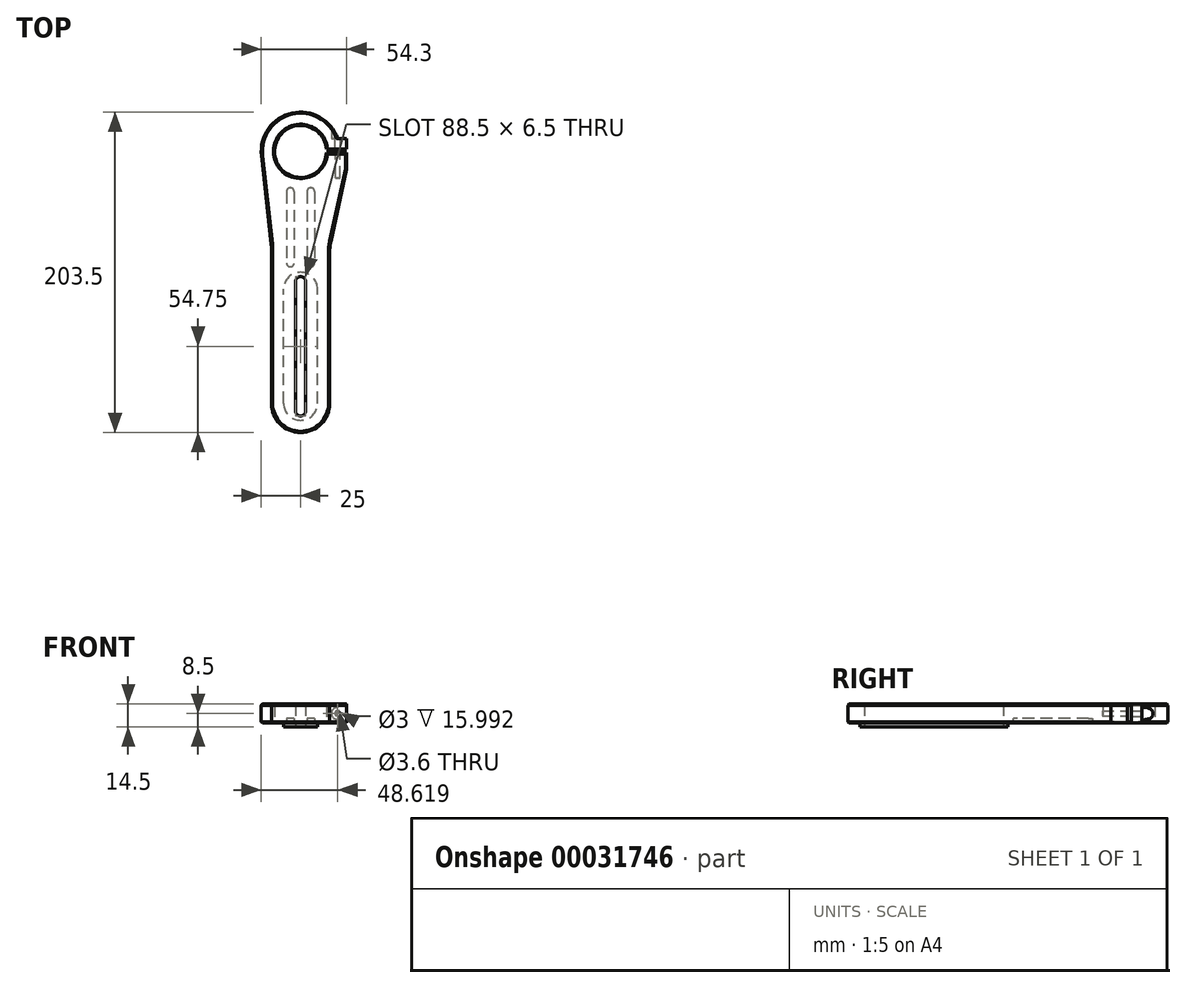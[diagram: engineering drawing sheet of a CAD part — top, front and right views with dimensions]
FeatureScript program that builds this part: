
annotation { "Feature Type Name" : "Feature", "Feature Type Description" : "" }
export const myFeature = defineFeature(function(context is Context, id is Id, definition is map)
    precondition{}
    {
        {
            var Q0;
            Q0=qCreatedBy(makeId("Top.planeOp"),FACE);
            var sketch = newSketch(context, id + "F0", { "sketchPlane" : qUnion([Q0])});
            skLineSegment(sketch, "E0.left", {"start": v(0, 0) * mm, "end": v(0, 99.61) * mm});
            skLineSegment(sketch, "E0.right", {"start": v(37, 0) * mm, "end": v(37, 99.61) * mm});
            skArc(sketch, "E1", {"start": v(0, 0) * mm, "mid": v(18.5, -18.5) * mm, "end": v(37, 0) * mm});
            skLineSegment(sketch, "E2", {"start": v(0, 99.61) * mm, "end": v(-6.35, 157.26) * mm});
            skArc(sketch, "E3", {"start": v(34.92, 161.59) * mm, "mid": v(2, 159.61) * mm, "end": v(34.98, 159.19) * mm});
            skLineSegment(sketch, "E4", {"start": v(34.92, 161.59) * mm, "end": v(47.8, 161.59) * mm});
            skLineSegment(sketch, "E5", {"start": v(34.98, 159.19) * mm, "end": v(47.8, 159.19) * mm});
            skArc(sketch, "E6.trimOffspring", {"start": v(42.12, 168.2) * mm, "mid": v(13, 184.39) * mm, "end": v(-6.35, 157.26) * mm});
            skLineSegment(sketch, "E7.trimOffspring", {"start": v(47.8, 159.19) * mm, "end": v(47.8, 148.78) * mm});
            skLineSegment(sketch, "E8", {"start": v(37, 99.61) * mm, "end": v(47.8, 148.78) * mm});
            skLineSegment(sketch, "E9", {"start": v(47.8, 168.2) * mm, "end": v(42.12, 168.2) * mm});
            skLineSegment(sketch, "E10", {"start": v(47.8, 168.2) * mm, "end": v(47.8, 161.59) * mm});
            skSolve(sketch);
        }
        {
            var Q0;
            Q0=makeQuery(id+"F0.imprint","IMPRINT",FACE,{"disambiguationData":[TD([[makeQuery(id+"F0.imprint","IMPRINT",EDGE,{"derivedFrom":sQuery(id+"F0.wireOp",EDGE,"E0.left")}),-1.0]])]});
            extrude(context, id + "F1", {"entities" : qUnion([Q0]), "depth" : 12 * mm});
        }
        {
            var Q0;
            Q0=makeQuery(id+"F1.opExtrude","CAP_FACE",FACE,{"disambiguationData":[OSD([sQuery(id+"F0.wireOp",EDGE,"E0.left"),sQuery(id+"F0.wireOp",EDGE,"E0.right"),sQuery(id+"F0.wireOp",EDGE,"E1"),sQuery(id+"F0.wireOp",EDGE,"17b39365-8552-41ff-bf17-2f0143301558"),sQuery(id+"F0.wireOp",EDGE,"c914b5d8-53f2-4ac4-93b2-2ecc952be14a")])],"isStart":true});
            var sketch = newSketch(context, id + "F2", { "sketchPlane" : qUnion([Q0])});
            skLineSegment(sketch, "E11.left", {"start": v(7.7, 0) * mm, "end": v(7.7, -72.5) * mm});
            skLineSegment(sketch, "E11.right", {"start": v(29.3, 0) * mm, "end": v(29.3, -72.5) * mm});
            skLineSegment(sketch, "E12", {"start": v(18.5, 153.67) * mm, "end": v(18.5, -165.42) * mm, "construction": true});
            skArc(sketch, "E13", {"start": v(29.3, 0) * mm, "mid": v(18.5, 10.8) * mm, "end": v(7.7, 0) * mm});
            skArc(sketch, "E14", {"start": v(7.7, -72.5) * mm, "mid": v(18.5, -83.3) * mm, "end": v(29.3, -72.5) * mm});
            skSolve(sketch);
        }
        {
            var Q0;
            Q0=qSketchRegion(id+"F2",true);
            extrude(context, id + "F3", {"entities" : qUnion([Q0]), "operationType" : NewBodyOperationType.ADD, "depth" : 2.5 * mm});
        }
        {
            var Q0;
            Q0=makeQuery(id+"F3.opExtrude","CAP_FACE",FACE,{"disambiguationData":[OSD([sQuery(id+"F2.wireOp",EDGE,"E11.left"),sQuery(id+"F2.wireOp",EDGE,"E11.right"),sQuery(id+"F2.wireOp",EDGE,"E13"),sQuery(id+"F2.wireOp",EDGE,"E14")])],"isStart":false});
            var sketch = newSketch(context, id + "F4", { "sketchPlane" : qUnion([Q0])});
            skLineSegment(sketch, "E15.left", {"start": v(15.25, 4.75) * mm, "end": v(15.25, -77.25) * mm});
            skLineSegment(sketch, "E15.right", {"start": v(21.75, 4.75) * mm, "end": v(21.75, -77.25) * mm});
            skArc(sketch, "E16", {"start": v(21.75, 4.75) * mm, "mid": v(18.5, 8) * mm, "end": v(15.25, 4.75) * mm});
            skArc(sketch, "E17", {"start": v(15.25, -77.25) * mm, "mid": v(18.5, -80.5) * mm, "end": v(21.75, -77.25) * mm});
            skPoint(sketch, "E18", {"position": v(18.5, 10.8) * mm});
            skLineSegment(sketch, "E19", {"start": v(-85.18, -36.25) * mm, "end": v(153.6, -36.25) * mm, "construction": true});
            skSolve(sketch);
        }
        {
            var Q0;
            Q0=qSketchRegion(id+"F4",true);
            extrude(context, id + "F5", {"entities" : qUnion([Q0]), "operationType" : NewBodyOperationType.REMOVE, "oppositeDirection" : true, "depth" : 25 * mm});
        }
        {
            var Q0;
            Q0=makeQuery(id+"F1.opExtrude","SWEPT_EDGE",EDGE,{"disambiguationData":[OSD([sQuery(id+"F0.wireOp",EDGE,"E0.right"),sQuery(id+"F0.wireOp",EDGE,"40b90229-f8af-40e6-8f66-2352c48dfe3b")])]});
            var Q1;
            Q1=makeQuery(id+"F1.opExtrude","SWEPT_EDGE",EDGE,{"disambiguationData":[OSD([sQuery(id+"F0.wireOp",EDGE,"E0.left"),sQuery(id+"F0.wireOp",EDGE,"5c4eed8a-842c-4bd0-9d32-765b3be9a9a6")])]});
            fillet(context, id + "F6", {"entities" : qUnion([Q0, Q1]), "radius" : 30 * mm, "tangentPropagation" : true, "allowEdgeOverflow" : false});
        }
        {
            var Q0;
            Q0=makeQuery(id+"F1.opExtrude","SWEPT_FACE",FACE,{"disambiguationData":[OSD([sQuery(id+"F0.wireOp",EDGE,"E9")])]});
            var sketch = newSketch(context, id + "F7", { "sketchPlane" : qUnion([Q0])});
            skCircle(sketch, "E20", {"center": v(-42.12, 6) * mm, "radius": 1.5 * mm});
            skSolve(sketch);
        }
        {
            var Q0;
            {var subQ0=makeQuery(id+"F1.opExtrude","SWEPT_EDGE",EDGE,{"disambiguationData":[OSD([sQuery(id+"F0.wireOp",EDGE,"E6.trimOffspring"),sQuery(id+"F0.wireOp",EDGE,"E9")])]});var subQ1=sQuery(id+"F7.wireOp",EDGE,"E20");var subQ3=makeQuery(id+"F7.imprint","INTERSECT",VERTEX,{"disambiguationData":[OD(0.0)],"derivedFrom":[subQ0,subQ1]});Q0=makeQuery(id+"F7.imprint","IMPRINT",FACE,{"disambiguationData":[TD([[makeQuery(id+"F7.imprint","IMPRINT",EDGE,{"disambiguationData":[TD([[subQ3,-1.0]])],"derivedFrom":subQ1}),1.0]])]});}
            var Q1;
            {var subQ0=makeQuery(id+"F1.opExtrude","SWEPT_EDGE",EDGE,{"disambiguationData":[OSD([sQuery(id+"F0.wireOp",EDGE,"E6.trimOffspring"),sQuery(id+"F0.wireOp",EDGE,"E9")])]});var subQ1=sQuery(id+"F7.wireOp",EDGE,"E20");var subQ3=makeQuery(id+"F7.imprint","INTERSECT",VERTEX,{"disambiguationData":[OD(0.0)],"derivedFrom":[subQ0,subQ1]});Q1=makeQuery(id+"F7.imprint","IMPRINT",FACE,{"disambiguationData":[TD([[makeQuery(id+"F7.imprint","IMPRINT",EDGE,{"disambiguationData":[TD([[subQ3,1.0]])],"derivedFrom":subQ1}),1.0]])]});}
            extrude(context, id + "F8", {"entities" : qUnion([Q0, Q1]), "operationType" : NewBodyOperationType.REMOVE, "oppositeDirection" : true, "depth" : 25 * mm, "hasSecondDirection" : true, "secondDirectionOppositeDirection" : false, "secondDirectionDepth" : 25 * mm});
        }
        {
            var Q0;
            Q0=makeQuery(id+"F1.opExtrude","SWEPT_FACE",FACE,{"disambiguationData":[OSD([sQuery(id+"F0.wireOp",EDGE,"E9")])]});
            var sketch = newSketch(context, id + "F9", { "sketchPlane" : qUnion([Q0])});
            skCircle(sketch, "E21", {"center": v(-42.12, 6) * mm, "radius": 4 * mm});
            skSolve(sketch);
        }
        {
            var Q0;
            Q0 = qSketchRegion(id + "F9", true);
            extrude(context, id + "F10", {"entities" : qUnion([Q0]), "operationType" : NewBodyOperationType.REMOVE, "depth" : 25 * mm});
        }
        {
            var Q0;
            Q0=makeQuery(id+"F10.boolean.opBoolean","MERGE",FACE,{"derivedFrom":[makeQuery(id+"F1.opExtrude","SWEPT_FACE",FACE,{"disambiguationData":[OSD([sQuery(id+"F0.wireOp",EDGE,"E9")])]}),makeQuery(id+"F10.opExtrude","CAP_FACE",FACE,{"disambiguationData":[OSD([sQuery(id+"F9.wireOp",EDGE,"E21")])],"isStart":true})]});
            var sketch = newSketch(context, id + "F11", { "sketchPlane" : qUnion([Q0])});
            skCircle(sketch, "E22", {"center": v(-42.12, 6) * mm, "radius": 1.8 * mm});
            skSolve(sketch);
        }
        {
            var Q0;
            Q0 = qSketchRegion(id + "F11", true);
            extrude(context, id + "F12", {"entities" : qUnion([Q0]), "operationType" : NewBodyOperationType.REMOVE, "oppositeDirection" : true, "depth" : 7.5 * mm});
        }
        {
            var Q0;
            Q0=makeQuery(id+"F1.opExtrude","CAP_EDGE",EDGE,{"disambiguationData":[OSD([sQuery(id+"F0.wireOp",EDGE,"E0.right")])],"isStart":false});
            var Q1;
            Q1=makeQuery(id+"F1.opExtrude","CAP_EDGE",EDGE,{"disambiguationData":[OSD([sQuery(id+"F0.wireOp",EDGE,"E5")])],"isStart":false});
            var Q2;
            Q2=makeQuery(id+"F1.opExtrude","CAP_EDGE",EDGE,{"disambiguationData":[OSD([sQuery(id+"F0.wireOp",EDGE,"E3")])],"isStart":false});
            var Q3;
            Q3=makeQuery(id+"F1.opExtrude","CAP_EDGE",EDGE,{"disambiguationData":[OSD([sQuery(id+"F0.wireOp",EDGE,"E7.trimOffspring")])],"isStart":false});
            chamfer(context, id + "F13", {"entities" : qUnion([Q0, Q1, Q2, Q3]), "width" : .75 * mm, "tangentPropagation" : true});
        }
        {
            var Q0;
            Q0=makeQuery(id+"F1.opExtrude","CAP_EDGE",EDGE,{"disambiguationData":[OSD([sQuery(id+"F0.wireOp",EDGE,"E3")])],"isStart":true});
            chamfer(context, id + "F14", {"entities" : qUnion([Q0]), "width" : .75 * mm, "tangentPropagation" : true});
        }
        {
            var Q0;
            Q0=makeQuery(id+"F1.opExtrude","CAP_EDGE",EDGE,{"disambiguationData":[OSD([sQuery(id+"F0.wireOp",EDGE,"E8")])],"isStart":true});
            chamfer(context, id + "F15", {"entities" : qUnion([Q0]), "width" : .75 * mm, "tangentPropagation" : true});
        }
        {
            var Q0;
            Q0=makeQuery(id+"F1.opExtrude","CAP_FACE",FACE,{"disambiguationData":[OSD([sQuery(id+"F0.wireOp",EDGE,"E0.left"),sQuery(id+"F0.wireOp",EDGE,"E0.right"),sQuery(id+"F0.wireOp",EDGE,"E1"),sQuery(id+"F0.wireOp",EDGE,"E2"),sQuery(id+"F0.wireOp",EDGE,"E3"),sQuery(id+"F0.wireOp",EDGE,"E4"),sQuery(id+"F0.wireOp",EDGE,"E5"),sQuery(id+"F0.wireOp",EDGE,"E6.trimOffspring"),sQuery(id+"F0.wireOp",EDGE,"E7.trimOffspring"),sQuery(id+"F0.wireOp",EDGE,"E8"),sQuery(id+"F0.wireOp",EDGE,"E9"),sQuery(id+"F0.wireOp",EDGE,"E10")])],"isStart":true});
            var sketch = newSketch(context, id + "F16", { "sketchPlane" : qUnion([Q0])});
            skLineSegment(sketch, "E23.bottom", {"start": v(27.5, -136.92) * mm, "end": v(22.5, -136.92) * mm});
            skLineSegment(sketch, "E23.top", {"start": v(27.5, -86.78) * mm, "end": v(22.5, -86.78) * mm});
            skLineSegment(sketch, "E23.left", {"start": v(27.5, -136.92) * mm, "end": v(27.5, -86.78) * mm});
            skLineSegment(sketch, "E23.right", {"start": v(22.5, -136.92) * mm, "end": v(22.5, -86.78) * mm});
            skLineSegment(sketch, "E24.bottom", {"start": v(14.5, -136.92) * mm, "end": v(9.5, -136.92) * mm});
            skLineSegment(sketch, "E24.top", {"start": v(14.5, -86.78) * mm, "end": v(9.5, -86.78) * mm});
            skLineSegment(sketch, "E24.left", {"start": v(14.5, -136.92) * mm, "end": v(14.5, -86.78) * mm});
            skLineSegment(sketch, "E24.right", {"start": v(9.5, -136.92) * mm, "end": v(9.5, -86.78) * mm});
            skLineSegment(sketch, "E25", {"start": v(18.5, -160) * mm, "end": v(18.5, 10.8) * mm, "construction": true});
            skSolve(sketch);
        }
        {
            var Q0;
            Q0 = qSketchRegion(id + "F16", true);
            extrude(context, id + "F17", {"entities" : qUnion([Q0]), "operationType" : NewBodyOperationType.REMOVE, "oppositeDirection" : true, "depth" : 3 * mm});
        }
        {
            var Q0;
            Q0=makeQuery(id+"F17.boolean.opBoolean","COPY",EDGE,{"derivedFrom":makeQuery(id+"F17.opExtrude","SWEPT_EDGE",EDGE,{"disambiguationData":[OSD([sQuery(id+"F16.wireOp",EDGE,"E23.bottom"),sQuery(id+"F16.wireOp",EDGE,"E23.right")])]})});
            var Q1;
            Q1=makeQuery(id+"F17.boolean.opBoolean","COPY",EDGE,{"derivedFrom":makeQuery(id+"F17.opExtrude","SWEPT_EDGE",EDGE,{"disambiguationData":[OSD([sQuery(id+"F16.wireOp",EDGE,"E23.bottom"),sQuery(id+"F16.wireOp",EDGE,"E23.left")])]})});
            var Q2;
            Q2=makeQuery(id+"F17.boolean.opBoolean","COPY",EDGE,{"derivedFrom":makeQuery(id+"F17.opExtrude","SWEPT_EDGE",EDGE,{"disambiguationData":[OSD([sQuery(id+"F16.wireOp",EDGE,"E24.bottom"),sQuery(id+"F16.wireOp",EDGE,"E24.left")])]})});
            var Q3;
            Q3=makeQuery(id+"F17.boolean.opBoolean","COPY",EDGE,{"derivedFrom":makeQuery(id+"F17.opExtrude","SWEPT_EDGE",EDGE,{"disambiguationData":[OSD([sQuery(id+"F16.wireOp",EDGE,"E24.bottom"),sQuery(id+"F16.wireOp",EDGE,"E24.right")])]})});
            var Q4;
            Q4=makeQuery(id+"F17.boolean.opBoolean","COPY",EDGE,{"derivedFrom":makeQuery(id+"F17.opExtrude","SWEPT_EDGE",EDGE,{"disambiguationData":[OSD([sQuery(id+"F16.wireOp",EDGE,"E24.top"),sQuery(id+"F16.wireOp",EDGE,"E24.right")])]})});
            var Q5;
            Q5=makeQuery(id+"F17.boolean.opBoolean","COPY",EDGE,{"derivedFrom":makeQuery(id+"F17.opExtrude","SWEPT_EDGE",EDGE,{"disambiguationData":[OSD([sQuery(id+"F16.wireOp",EDGE,"E24.top"),sQuery(id+"F16.wireOp",EDGE,"E24.left")])]})});
            var Q6;
            Q6=makeQuery(id+"F17.boolean.opBoolean","COPY",EDGE,{"derivedFrom":makeQuery(id+"F17.opExtrude","SWEPT_EDGE",EDGE,{"disambiguationData":[OSD([sQuery(id+"F16.wireOp",EDGE,"E23.top"),sQuery(id+"F16.wireOp",EDGE,"E23.left")])]})});
            var Q7;
            Q7=makeQuery(id+"F17.boolean.opBoolean","COPY",EDGE,{"derivedFrom":makeQuery(id+"F17.opExtrude","SWEPT_EDGE",EDGE,{"disambiguationData":[OSD([sQuery(id+"F16.wireOp",EDGE,"E23.top"),sQuery(id+"F16.wireOp",EDGE,"E23.right")])]})});
            fillet(context, id + "F18", {"entities" : qUnion([Q0, Q1, Q2, Q3, Q4, Q5, Q6, Q7]), "radius" : 2.5 * mm, "tangentPropagation" : true, "allowEdgeOverflow" : false});
        }
    });
